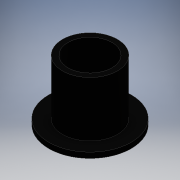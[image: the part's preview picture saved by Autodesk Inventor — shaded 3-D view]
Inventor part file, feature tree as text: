
AUTODESK INVENTOR PART (.ipt)
format: ipt  version: 2016 (Build 200138000, 138)  size: 101,888 bytes
history: native  units: mm
features: extrude x2, other x1, sketch x1
ambient origin geometry x8: Origin, YZ Plane, XZ Plane, XY Plane, X Axis, Y Axis, Z Axis, Center Point
bodies: Body1 (feature_tree)
feature tree (4):
  other  "ソリッド1"
  sketch  "スケッチ1"
  extrude  "押し出し1"  Depth=15.0mm
  extrude  "押し出し2"  Depth=10.0mm
